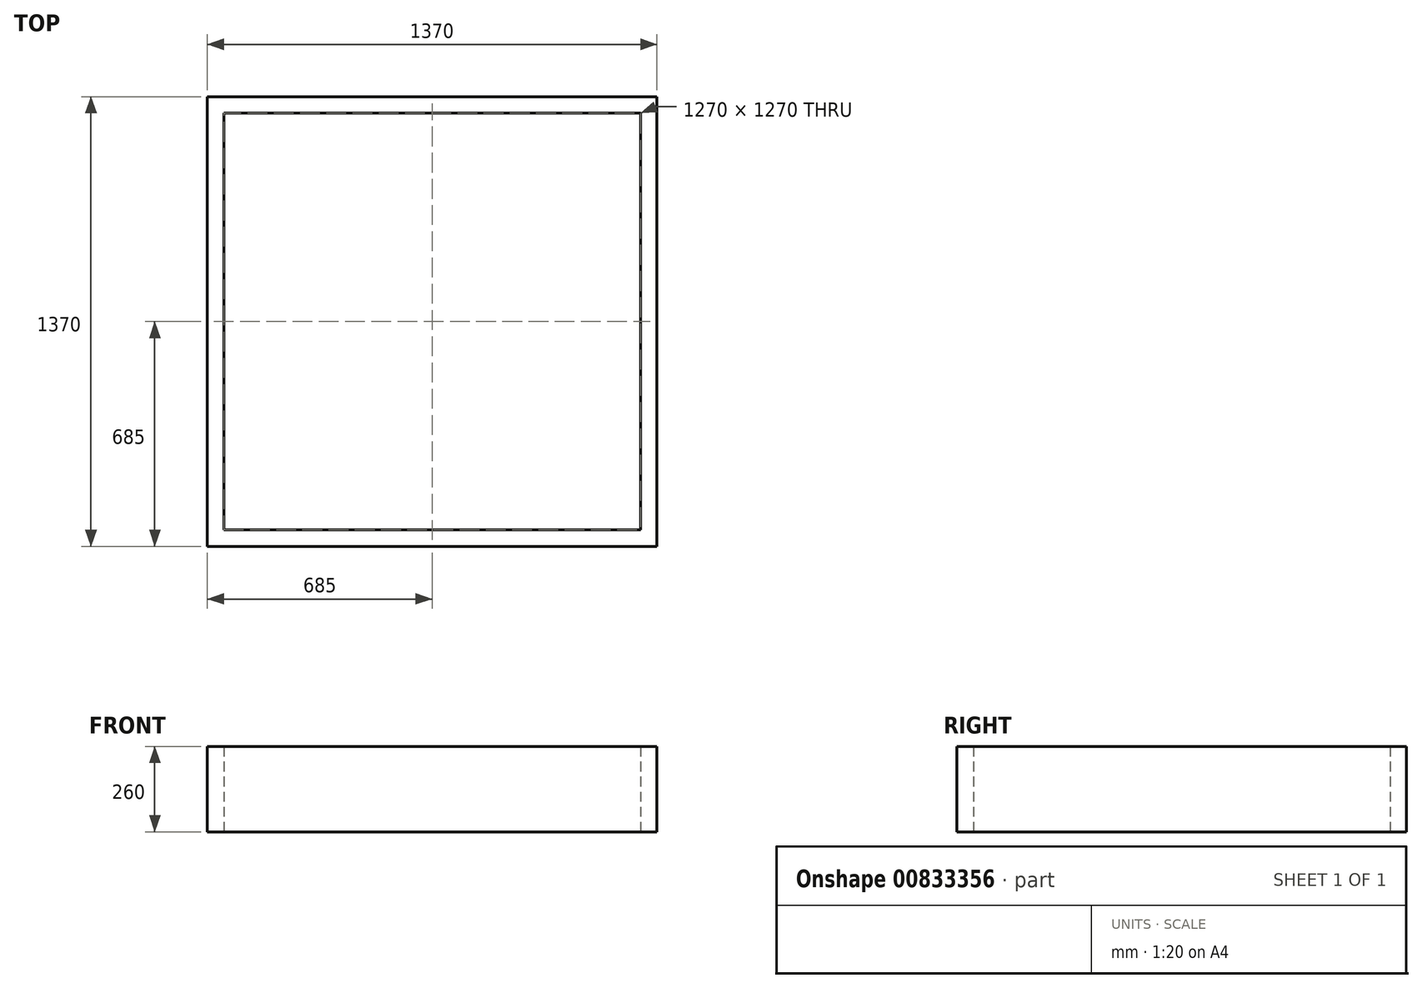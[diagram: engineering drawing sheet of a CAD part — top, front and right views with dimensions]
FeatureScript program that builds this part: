
annotation { "Feature Type Name" : "Feature", "Feature Type Description" : "" }
export const myFeature = defineFeature(function(context is Context, id is Id, definition is map)
    precondition{}
    {
        {
            var Q0;
            Q0=qCreatedBy(makeId("Top.planeOp"),FACE);
            var sketch = newSketch(context, id + "F0", { "sketchPlane" : qUnion([Q0])});
            skLineSegment(sketch, "E0.bottom", {"start": v(-635, 635) * mm, "end": v(635, 635) * mm});
            skLineSegment(sketch, "E0.top", {"start": v(-635, -635) * mm, "end": v(635, -635) * mm});
            skLineSegment(sketch, "E0.left", {"start": v(-635, 635) * mm, "end": v(-635, -635) * mm});
            skLineSegment(sketch, "E0.right", {"start": v(635, 635) * mm, "end": v(635, -635) * mm});
            skPoint(sketch, "E0.middle", {"position": v(0, 0) * mm});
            skLineSegment(sketch, "E1.0", {"start": v(-685, 685) * mm, "end": v(685, 685) * mm});
            skLineSegment(sketch, "E1.1", {"start": v(-685, 685) * mm, "end": v(-685, -685) * mm});
            skLineSegment(sketch, "E1.2", {"start": v(-685, -685) * mm, "end": v(685, -685) * mm});
            skLineSegment(sketch, "E1.3", {"start": v(685, 685) * mm, "end": v(685, -685) * mm});
            skSolve(sketch);
        }
        {
            var Q0;
            Q0=makeQuery(id+"F0.imprint","IMPRINT",FACE,{"disambiguationData":[TD([[makeQuery(id+"F0.imprint","IMPRINT",EDGE,{"derivedFrom":sQuery(id+"F0.wireOp",EDGE,"E0.bottom")}),1.0]])]});
            extrude(context, id + "F1", {"entities" : qUnion([Q0]), "depth" : 260 * mm, "offsetDistance" : 25 * mm});
        }
    });
